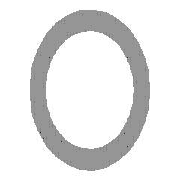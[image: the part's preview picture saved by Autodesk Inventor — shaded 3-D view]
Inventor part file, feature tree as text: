
AUTODESK INVENTOR PART (.ipt)
format: ipt  version: 2021 (Build 250183000, 183)  size: 280,064 bytes
history: native  units: mm (DEFAULTED — no unit token found)
features: other x13, plane x5, sketch x3, sweep x1, extrude x1
ambient origin geometry x8: Origin, YZ Plane, XZ Plane, XY Plane, X Axis, Y Axis, Z Axis, Center Point
bodies: Solid1 (feature_tree)
feature tree (23):
  parser-record x1  (decoder bookkeeping rows leaked as tree rows — omitted from the tree; the rows remain in map.json)
  other  "Driven Length"
  other  "Plano inicial"
  other  "Plano final"
  other  "Trayectoria de barrido"
  plane  "Plano de trabajo de orientación"
  sweep  "Cuerpo"
  plane  "Plano de trabajo5"
  plane  "Plano de trabajo6"
  plane  "Plano de trabajo7"
  extrude  "Extrusión2"  Depth=739.165161mm
  other  "Combinar5"
  sketch  "Sketch3"  dims[d0=33.528mm d1=4.5466mm]
  plane  "Work Plane3"
  sketch  "Sketch4"  dims[d4=-0.0mm d5=739.165161mm]
  sketch  "Boceto5"  dims[d6=90.0deg d7=739.165161mm d8=0.0mm d9=0.0mm d26=0.12mm d27=0.0mm d204=5.0mm d205=0.0mm d206=5.0mm d207=0.0mm]
  other  "Sólido6"
  other  "Sup146"
  other  "Sup147"
  other  "Sólido51"
  other  "Sup145"
  other  "Superficie de contorno97"
  other  "Superficie de contorno98"
